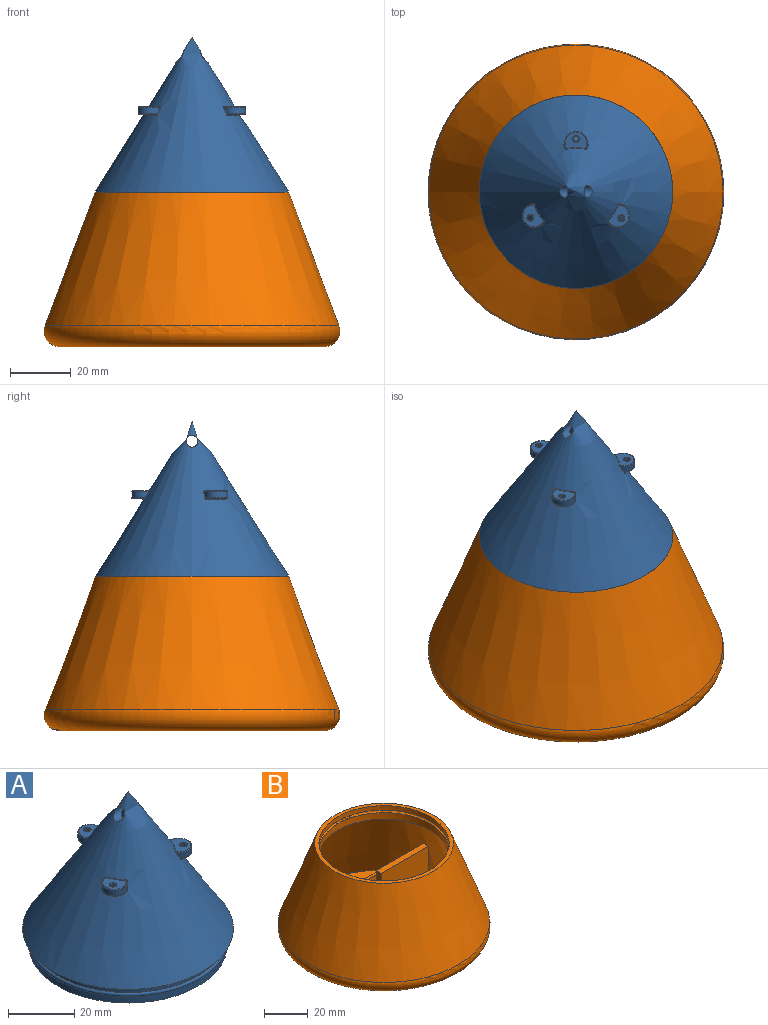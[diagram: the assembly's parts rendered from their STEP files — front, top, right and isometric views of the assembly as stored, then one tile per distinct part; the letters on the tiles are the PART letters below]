
ASSEMBLY  parts=2 mates=1
PART A: 54 faces, bbox 66x66x57.2 mm
  f0: cone r=0mm half-angle=32deg, axis (0,0,-1), area 5863.7mm2, adj f6,f8,f21,f23,f24,f25,f26,f28
  f1: cylinder r=29.84mm len=59.69mm, axis (0,0,1), area 476.3mm2, adj f3,f5
  f2: cylinder r=28.75mm len=57.51mm, axis (0,0,1), area 1147.3mm2, adj f3,f4
  f3: plane 59.69x59.69mm, normal (0,0,-1), area 200.7mm2, adj f1,f2
  f4: cone r=0mm half-angle=32deg, axis (0,0,-1), area 4877.5mm2, adj f2,f8
  f5: torus R=29.86mm, axis (0,0,-1), area 384.5mm2, adj f1,f7
  f6: plane 63.5x63.5mm, normal (0,0,-1), area 368.6mm2, adj f0,f7
  f7: cylinder r=29.84mm len=59.69mm, axis (0,0,1), area 476.3mm2, adj f5,f6
  f8: cylinder r=1.94mm len=10.63mm, axis (1,0,0), area 79.8mm2, adj f0,f4
  f9: cylinder r=3.81mm len=7.62mm, axis (0,0,-1), area 28.4mm2, adj f41,f44,f47,f50
  f10: plane 7.11x5.39mm, normal (0,0,1), area 26.9mm2, adj f44,f45,f53
  f11: plane 7.11x3.55mm, normal (0,0,-1), area 15.5mm2, adj f20,f46,f47
  f12: cylinder r=3.81mm len=7.6mm, axis (0,0,-1), area 28.4mm2, adj f22,f25,f26,f27
  f13: plane 7.11x6.67mm, normal (0,0,1), area 26.9mm2, adj f21,f22,f52
  f14: plane 6.63x5.33mm, normal (0,0,-1), area 15.5mm2, adj f19,f27,f30
  f15: cylinder r=3.81mm len=7.6mm, axis (0,0,-1), area 28.4mm2, adj f31,f34,f37,f40
  f16: plane 7.11x6.67mm, normal (0,0,1), area 26.9mm2, adj f36,f37,f51
  f17: plane 6.63x5.33mm, normal (0,0,-1), area 15.5mm2, adj f18,f34,f35
  f18: cylinder r=0.89mm len=2.29mm, axis (0,0,1), area 12.8mm2, adj f17,f51
  f19: cylinder r=0.89mm len=2.29mm, axis (0,0,1), area 12.8mm2, adj f14,f52
  f20: cylinder r=0.89mm len=2.29mm, axis (0,0,1), area 12.8mm2, adj f11,f53
  f21: torus R=14.43mm, axis (0,0,1), area 1.6mm2, adj f0,f13,f23,f24
  f22: torus R=3.56mm, axis (0,0,1), area 6.1mm2, adj f12,f13,f23,f24
  f23: bspline ~0.74x0.6mm, area 0.2mm2, adj f0,f21,f22,f25
  f24: bspline ~0.77x0.63mm, area 0.2mm2, adj f0,f21,f22,f26
  f25: bspline ~4.03x2.49mm, area 1mm2, adj f0,f12,f23,f28
  f26: bspline ~3.11x1.62mm, area 1mm2, adj f0,f12,f24,f29
  f27: torus R=3.56mm, axis (0,0,1), area 4.8mm2, adj f12,f14,f28,f29
  f28: bspline ~0.74x0.66mm, area 0.3mm2, adj f0,f25,f27,f30
  f29: bspline ~0.85x0.68mm, area 0.3mm2, adj f0,f26,f27,f30
  f30: torus R=16.33mm, axis (0,0,1), area 3.8mm2, adj f0,f14,f28,f29
  f31: bspline ~4.03x1.97mm, area 1mm2, adj f0,f15,f32,f33
  f32: bspline ~0.82x0.66mm, area 0.3mm2, adj f0,f31,f34,f35
  f33: bspline ~0.77x0.6mm, area 0.2mm2, adj f0,f31,f36,f37
  f34: torus R=3.56mm, axis (0,0,1), area 4.8mm2, adj f15,f17,f32,f38
  f35: torus R=16.33mm, axis (0,0,1), area 3.8mm2, adj f0,f17,f32,f38
  f36: torus R=14.43mm, axis (0,0,1), area 1.6mm2, adj f0,f16,f33,f39
  f37: torus R=3.56mm, axis (0,0,1), area 6.1mm2, adj f15,f16,f33,f39
  f38: bspline ~0.76x0.68mm, area 0.3mm2, adj f0,f34,f35,f40
  f39: bspline ~0.75x0.63mm, area 0.2mm2, adj f0,f36,f37,f40
  f40: bspline ~3.11x1.93mm, area 1mm2, adj f0,f15,f38,f39
  f41: bspline ~3.11x2.01mm, area 1mm2, adj f0,f9,f42,f43
  f42: bspline ~0.75x0.55mm, area 0.2mm2, adj f0,f41,f44,f45
  f43: bspline ~0.72x0.68mm, area 0.3mm2, adj f0,f41,f46,f47
  f44: torus R=3.56mm, axis (0,0,1), area 6.1mm2, adj f9,f10,f42,f48
  f45: torus R=14.43mm, axis (0,0,1), area 1.6mm2, adj f0,f10,f42,f48
  f46: torus R=16.33mm, axis (0,0,1), area 3.8mm2, adj f0,f11,f43,f49
  f47: torus R=3.56mm, axis (0,0,1), area 4.8mm2, adj f9,f11,f43,f49
  f48: bspline ~0.76x0.6mm, area 0.2mm2, adj f0,f44,f45,f50
  f49: bspline ~0.68x0.66mm, area 0.3mm2, adj f0,f46,f47,f50
  f50: bspline ~4.03x2.55mm, area 1mm2, adj f0,f9,f48,f49
  f51: torus R=1.14mm, axis (0,0,1), area 2.5mm2, adj f16,f18
  f52: torus R=1.14mm, axis (0,0,1), area 2.5mm2, adj f13,f19
  f53: torus R=1.14mm, axis (0,0,1), area 2.5mm2, adj f10,f20
PART B: 41 faces, bbox 105.1x105.1x50.8 mm
  f0: plane 20.02x15.64mm, normal (0.79,0.62,0), area 127.7mm2, adj f1,f2,f22,f24,f33,f36
  f1: plane 36.03x28.15mm, normal (0.62,-0.79,0), area 231.2mm2, adj f0,f2,f23,f24,f31,f36
  f2: plane 94.27x94.27mm, normal (0,0,1), area 3986.9mm2, adj f0,f1,f8,f11,f12,f13,f14,f17
  f3: cylinder r=29.84mm len=59.69mm, axis (0,0,1), area 452.6mm2, adj f5,f7
  f4: cone r=31.75mm half-angle=20.6deg, axis (0,0,-1), area 11789.8mm2, adj f5,f37
  f5: plane 63.5x63.5mm, normal (0,0,1), area 368.6mm2, adj f3,f4
  f6: plane 86.94x86.94mm, normal (0,0,-1), area 4088mm2, adj f27,f28,f29,f30,f37,f38,f39,f40
  f7: torus R=29.82mm, axis (0,0,1), area 446.6mm2, adj f3,f10
  f8: cone r=29.37mm half-angle=20.6deg, axis (0,0,-1), area 10776.2mm2, adj f2,f9
  f9: plane 63.79x63.79mm, normal (0,0,-1), area 397.6mm2, adj f8,f10
  f10: cylinder r=29.84mm len=59.69mm, axis (0,0,1), area 690.7mm2, adj f7,f9
  f11: plane 28.58x2.54mm, normal (-1,0,0), area 72.6mm2, adj f2,f12,f14,f15
  f12: plane 50.8x2.54mm, normal (0,-1,0), area 129mm2, adj f2,f11,f13,f15
  f13: plane 28.58x2.54mm, normal (1,0,0), area 72.6mm2, adj f2,f12,f14,f15
  f14: plane 50.8x2.54mm, normal (0,1,0), area 129mm2, adj f2,f11,f13,f15
  f15: plane 50.8x28.58mm, normal (0,0,1), area 944.9mm2, adj f11,f12,f13,f14,f16
  f16: cylinder r=12.7mm len=25.4mm, axis (0,0,1), area 202.7mm2, adj f15,f40
  f17: plane 25.4x3.18mm, normal (-1,0,0), area 80.6mm2, adj f2,f18,f20,f21
  f18: plane 30.48x25.4mm, normal (0,-1,0), area 774.2mm2, adj f2,f17,f19,f21
  f19: plane 25.4x3.18mm, normal (1,0,0), area 80.6mm2, adj f2,f18,f20,f21
  f20: plane 30.48x25.4mm, normal (0,1,0), area 774.2mm2, adj f2,f17,f19,f21
  f21: plane 30.48x3.18mm, normal (0,0,1), area 96.8mm2, adj f17,f18,f19,f20
  f22: plane 36.03x28.15mm, normal (-0.62,0.79,0), area 232.3mm2, adj f0,f2,f23,f24
  f23: plane 20.02x15.64mm, normal (-0.79,-0.62,0), area 129mm2, adj f1,f2,f22,f24
  f24: plane 51.67x48.16mm, normal (0,0,1), area 591.2mm2, adj f0,f1,f22,f23,f25,f26
  f25: cylinder r=9.53mm len=19.05mm, axis (0,0,1), area 304mm2, adj f24,f38
  f26: cylinder r=9.53mm len=19.05mm, axis (0,0,1), area 304mm2, adj f24,f39
  f27: plane 14.29x5.08mm, normal (0,1,0), area 72.6mm2, adj f6,f28,f29,f36
  f28: plane 14.29x5.08mm, normal (1,0,0), area 72.6mm2, adj f6,f27,f30,f36
  f29: plane 14.29x5.08mm, normal (-1,0,0), area 72.6mm2, adj f6,f27,f30,f36
  f30: plane 14.29x5.08mm, normal (0,-1,0), area 72.6mm2, adj f6,f28,f29,f36
  f31: plane 6.58x2.54mm, normal (-1,0,0), area 16.7mm2, adj f1,f2,f34,f36
  f32: plane 16.83x2.54mm, normal (0,1,0), area 42.7mm2, adj f2,f33,f35,f36
  f33: plane 9.57x2.54mm, normal (-1,0,0), area 24.3mm2, adj f0,f2,f32,f36
  f34: plane 16.83x2.54mm, normal (0,-1,0), area 42.7mm2, adj f2,f31,f35,f36
  f35: plane 16.83x2.54mm, normal (1,0,0), area 42.7mm2, adj f2,f32,f34,f36
  f36: plane 16.83x16.83mm, normal (0,0,1), area 78.9mm2, adj f0,f1,f27,f28,f29,f30,f31,f32
  f37: torus R=43.47mm, axis (0,0,1), area 2896.3mm2, adj f4,f6
  f38: torus R=12.06mm, axis (0,0,1), area 261.9mm2, adj f6,f25
  f39: torus R=12.06mm, axis (0,0,1), area 261.9mm2, adj f6,f26
  f40: torus R=15.24mm, axis (0,0,1), area 341.5mm2, adj f6,f16
PLACE A t=(-30.76,-7.44,4.02)mm
PLACE B t=(-30.76,-7.44,-46.78)mm
MATE fastened A.f0 <-> B.f3  axis (0,0,-1) through (-30.76,-7.44,4.02)mm
